# Revit family: Electronics_Commercial-Loudspeakers_Biamp_Bidirectional-Sound-Projector_EN-MPBD5T10-W
name_source: partatom
category: Communication Devices
units: mm (PartAtom-declared; Revit-internal decimal feet)

## family parameters
Cut with Voids When Loaded = No
Host = Face
Maintain Annotation Orientation = No
OmniClass Number = 23.85.10.11.14.14.14
OmniClass Title = Loudspeakers
Part Type = Normal
Room Calculation Point = No
Round Connector Dimension = Use Diameter
Shared = No

## types (1)
- EN-MPBD5T10-W
    100V transformer power taps in watts = 10 - 6 - 3 - 1.5
    Certificate ref = 1438/CPR/0356
    Closest RAL colour (subject to deviations) = RAL9010
    Colour = White
    Connector Description = Conductor; 10-6-3-1.5 W 100V
    Default Elevation = 48 "
    Depth = 6 "
    Description = EN-MPBD5T10-W EN54-24 Certified 2 x 5 Bidirectional Sound Projector
    Diameter = 6 "
    Frequency response in Hz = 145 - 17.5 k
    Grill Material = Biamp - Plastic - White(Grid)
    Housing Material = Biamp - Plastic - White
    IP rating = 54
    Loudspeaker system = Full range
    Main construction material = Aluminium
    Manufacturer = Biamp
    Max SPL 1m in dB = 104
    Model = EN-MPBD5T10-W
    Mounting system = 2 screws
    Operating temperatures = -25°C to 70°C
    Product Documentation Link = https://downloads.biamp.com
    Product Page URL = https://www.biamp.com
    Product data url = https://bimobject.com
    SPL 1W/1m in dB = 94
    URL = https://www.biamp.com
    Version = 1
    Vertical dispersion angle 1000 Hz = 155°
    Weight = 5.11 lb
    Woofer cone material = Coated paper
    Woofer size in inch = 2 x 5.25

## geometry (parser evidence)
native form markers: Sweep x6
no freeform markers — native parametric forms only
